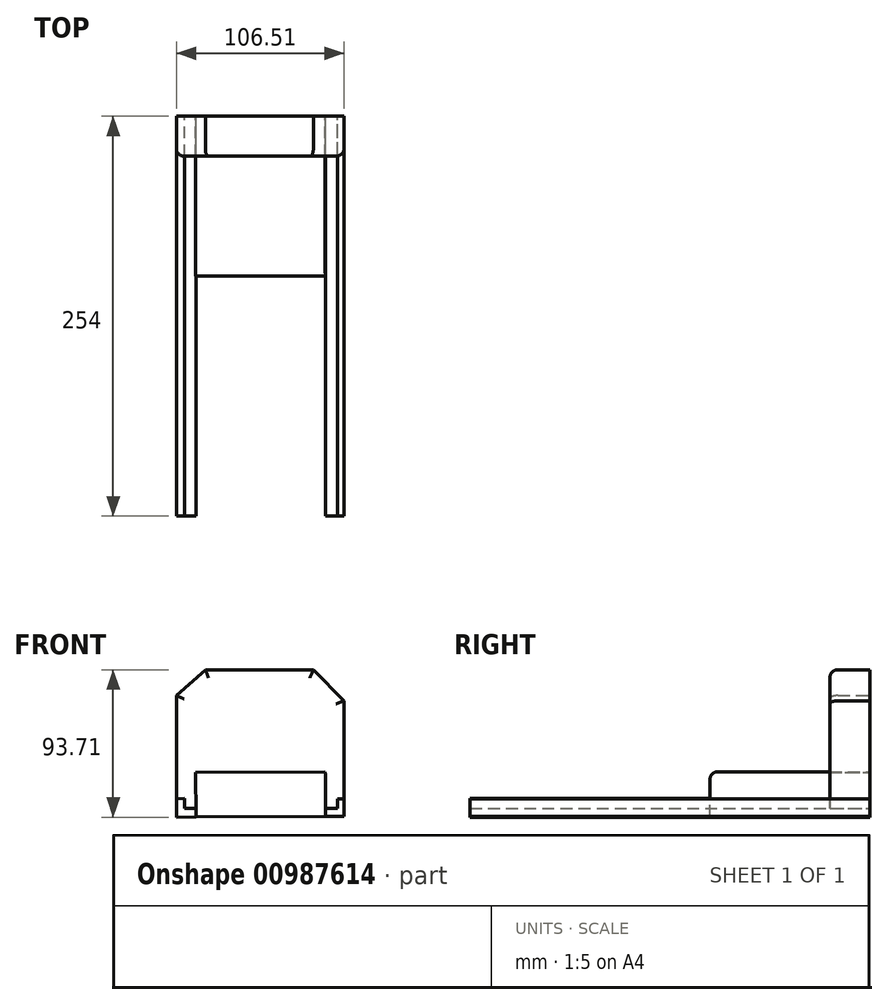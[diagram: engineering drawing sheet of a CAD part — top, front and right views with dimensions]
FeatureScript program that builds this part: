
annotation { "Feature Type Name" : "Feature", "Feature Type Description" : "" }
export const myFeature = defineFeature(function(context is Context, id is Id, definition is map)
    precondition{}
    {
        {
            var Q0;
            Q0=qCreatedBy(makeId("Front.planeOp"),FACE);
            var sketch = newSketch(context, id + "F0", { "sketchPlane" : qUnion([Q0])});
            skLineSegment(sketch, "E0", {"start": v(-34.7, 64.78) * mm, "end": v(33.92, 64.78) * mm});
            skLineSegment(sketch, "E1", {"start": v(33.92, 64.78) * mm, "end": v(53.38, 45.06) * mm});
            skLineSegment(sketch, "E2", {"start": v(53.38, 45.06) * mm, "end": v(53.38, -28.42) * mm});
            skLineSegment(sketch, "E3", {"start": v(-34.7, 64.78) * mm, "end": v(-53.13, 48.4) * mm});
            skLineSegment(sketch, "E4", {"start": v(-53.13, 48.4) * mm, "end": v(-53.13, -28.93) * mm});
            skLineSegment(sketch, "E5", {"start": v(-53.13, -28.93) * mm, "end": v(53.38, -28.42) * mm});
            skLineSegment(sketch, "E6", {"start": v(41.6, -28.48) * mm, "end": v(41.47, 0) * mm});
            skLineSegment(sketch, "E7", {"start": v(41.47, 0) * mm, "end": v(-40.83, -0.4) * mm});
            skLineSegment(sketch, "E8", {"start": v(-40.83, -0.4) * mm, "end": v(-40.7, -28.87) * mm});
            skLineSegment(sketch, "E9", {"start": v(53.38, -17.15) * mm, "end": v(49.29, -17.15) * mm});
            skLineSegment(sketch, "E10", {"start": v(49.29, -17.15) * mm, "end": v(49.32, -23.3) * mm});
            skLineSegment(sketch, "E11", {"start": v(49.32, -23.3) * mm, "end": v(41.58, -23.34) * mm});
            skLineSegment(sketch, "E12", {"start": v(41.58, -23.34) * mm, "end": v(41.6, -28.48) * mm});
            skLineSegment(sketch, "E13", {"start": v(-53.13, -17.15) * mm, "end": v(-48, -17.13) * mm});
            skLineSegment(sketch, "E14", {"start": v(-48, -17.13) * mm, "end": v(-47.98, -23.34) * mm});
            skLineSegment(sketch, "E15", {"start": v(-47.98, -23.34) * mm, "end": v(-40.24, -23.3) * mm});
            skSolve(sketch);
        }
        {
            var Q0;
            {var subQ0=sQuery(id+"F0.wireOp",EDGE,"E13");Q0=makeQuery(id+"F0.imprint","IMPRINT",FACE,{"disambiguationData":[TD([[makeQuery(id+"F0.imprint","IMPRINT",EDGE,{"derivedFrom":subQ0}),-1.0]])]});}
            var Q1;
            {var subQ0=sQuery(id+"F0.wireOp",EDGE,"E9");Q1=makeQuery(id+"F0.imprint","IMPRINT",FACE,{"disambiguationData":[TD([[makeQuery(id+"F0.imprint","IMPRINT",EDGE,{"derivedFrom":subQ0}),1.0]])]});}
            extrude(context, id + "F1", {"entities" : qUnion([Q0, Q1]), "depth" : 254 * mm, "offsetDistance" : 25.4 * mm});
        }
        {
            var Q0;
            Q0=makeQuery(id+"F0.imprint","IMPRINT",FACE,{"disambiguationData":[TD([[makeQuery(id+"F0.imprint","IMPRINT",EDGE,{"derivedFrom":sQuery(id+"F0.wireOp",EDGE,"E6")}),1.0]])]});
            extrude(context, id + "F2", {"entities" : qUnion([Q0]), "depth" : 101.6 * mm, "offsetDistance" : 25.4 * mm});
        }
        {
            var Q0;
            Q0=makeQuery(id+"F0.imprint","IMPRINT",FACE,{"disambiguationData":[TD([[makeQuery(id+"F0.imprint","IMPRINT",EDGE,{"derivedFrom":sQuery(id+"F0.wireOp",EDGE,"E0")}),-1.0]])]});
            extrude(context, id + "F3", {"entities" : qUnion([Q0]), "depth" : 25.4 * mm, "offsetDistance" : 25.4 * mm});
        }
        {
            var Q0;
            Q0=makeQuery(id+"F2.opExtrude","SWEPT_FACE",FACE,{"disambiguationData":[OSD([sQuery(id+"F0.wireOp",EDGE,"E7")])]});
            var sketch = newSketch(context, id + "F4", { "sketchPlane" : qUnion([Q0])});
            skLineSegment(sketch, "E16", {"start": v(35.86, -28.6) * mm, "end": v(-34.57, -28.6) * mm});
            skLineSegment(sketch, "E17", {"start": v(-34.57, -28.6) * mm, "end": v(-34.57, -95.68) * mm});
            skLineSegment(sketch, "E18", {"start": v(35.86, -28.6) * mm, "end": v(35.86, -95.68) * mm});
            skLineSegment(sketch, "E19", {"start": v(35.86, -95.68) * mm, "end": v(-34.57, -95.68) * mm});
            skSolve(sketch);
        }
        {
            var Q0;
            Q0=makeQuery(id+"F3.opExtrude","CAP_EDGE",EDGE,{"disambiguationData":[OSD([sQuery(id+"F0.wireOp",EDGE,"E3")])],"isStart":false});
            var Q1;
            Q1=makeQuery(id+"F3.opExtrude","CAP_EDGE",EDGE,{"disambiguationData":[OSD([sQuery(id+"F0.wireOp",EDGE,"E0")])],"isStart":false});
            var Q2;
            Q2=makeQuery(id+"F3.opExtrude","CAP_EDGE",EDGE,{"disambiguationData":[OSD([sQuery(id+"F0.wireOp",EDGE,"E1")])],"isStart":false});
            var Q3;
            Q3=makeQuery(id+"F3.opExtrude","CAP_EDGE",EDGE,{"disambiguationData":[OSD([sQuery(id+"F0.wireOp",EDGE,"E2")])],"isStart":false});
            var Q4;
            Q4=makeQuery(id+"F2.opExtrude","CAP_EDGE",EDGE,{"disambiguationData":[OSD([sQuery(id+"F0.wireOp",EDGE,"E7")])],"isStart":false});
            var Q5;
            Q5=makeQuery(id+"F3.opExtrude","CAP_EDGE",EDGE,{"disambiguationData":[OSD([sQuery(id+"F0.wireOp",EDGE,"E4")])],"isStart":false});
            fillet(context, id + "F5", {"entities" : qUnion([Q0, Q1, Q2, Q3, Q4, Q5]), "radius" : 5.08 * mm, "tangentPropagation" : true, "allowEdgeOverflow" : false});
        }
        {
            var Q0;
            Q0=makeQuery(id+"F4.imprint","IMPRINT",FACE,{"disambiguationData":[TD([[makeQuery(id+"F4.imprint","IMPRINT",EDGE,{"derivedFrom":sQuery(id+"F4.wireOp",EDGE,"E16")}),1.0]])]});
            extrude(context, id + "F6", {"entities" : qUnion([Q0]), "operationType" : NewBodyOperationType.ADD, "oppositeDirection" : true, "depth" : 25.4 * mm, "offsetDistance" : 25.4 * mm});
        }
    });
